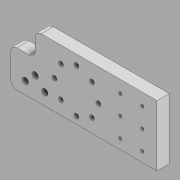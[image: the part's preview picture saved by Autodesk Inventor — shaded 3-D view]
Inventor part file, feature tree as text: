
AUTODESK INVENTOR PART (.ipt)
format: ipt  version: 2020 (Build 240168000, 168)  size: 141,824 bytes
history: native  units: in
note: dims shown in document units (in); Inventor stores cm internally (conversion verified against a paired STEP export)
features: sketch x4, hole x3, extrude x1, other x1, pattern_circular x1, pattern_linear x1, fillet x1
ambient origin geometry x8: Origin, YZ Plane, XZ Plane, XY Plane, X Axis, Y Axis, Z Axis, Center Point
bodies: Solid1 (feature_tree)
feature tree (12):
  extrude  "Extrusion1"  Depth=2.5in
  hole  "Hole1"  [1 undecoded]
  hole  "Hole2"  [1 undecoded]
  other  "Work Axis1"
  pattern_circular  "Circular Pattern1"  [2 undecoded]
  hole  "Hole3"  [1 undecoded]
  pattern_linear  "Rectangular Pattern1"  Spacing1=0.4in  [1 undecoded]
  fillet  "Fillet1"  Radius=1.8in
  sketch  "Sketch1"  dims[d0=6.0in d1=2.5in]
  sketch  "Sketch2"  dims[d2=5.0in d3=1.5in]
  sketch  "Sketch3"  dims[d4=0.5in d5=0.0in d6=5.0in]
  sketch  "Sketch4"  dims[d7=0.4in d8=0.5in d9=0.4in d10=0.4in d11=0.25in d12=0.75in d13=0.375in d14=0.25in d15=0.5635in d16=1.0in d17=0.8108in d18=1.8in d19=3.3in d20=1.2in d25=0.188in d26=0.75in d27=0.375in d28=0.25in d29=0.5635in d30=1.0in d31=0.8108in d32=1.5in d34=3.1496in d35=360.0deg d37=2.0in d38=0.125in d39=0.75in d40=0.375in d41=0.25in d42=0.5635in d43=1.0in d44=0.8108in d45=0.7874in d47=0.9in d48=1.1811in d50=0.8in d51=0.25in]
note: 6 required parameter values undecoded (feature->parameter linkage not recoverable at this tier; creation-order binding heuristic only, values carry confidence <= 0.55)
